# Revit family: RN 57035 Optifitt-Press-Übergang
name_source: partatom
category: Rohrformteile
units: mm (PartAtom-declared; Revit-internal decimal feet)

## family parameters
Arbeitsebenenbasiert = Nein
Beim Laden mit Abzugskörper schneiden = Nein
Bemaßung runder Anschluss = Durchmesser verwenden
Gemeinsam genutzt = Nein
Immer vertikal = Ja
Teiletyp = Verbindung

## types (8) — shared parameters
1.010.00.2 Blattnummer der Richtlinie = 29
1.010.00.3 Ausgabedatum (Monat) der Richtlinie = 201308
1.010.00.4 Herstellername = R. Nussbaum AG
1.010.00.5 Revisionsdatum der Datei = 20190521
1.010.00.6 Webadresse des Herstellers = http://www.nussbaum.ch
1.100.00.4 Produktbezeichnung = Versorgung
1.110.00.2 Index = 2
1.110.00.4 Produktbezeichnung = Optifitt-Press
1.960/3L.00.8 Link (URL) = https://www.nussbaum.ch
29.700.00.4 Produktname = Optifitt-Press-Übergang, mit Aussengewinde
29.700.00.5 Produktkennung = 2
29.700.00.6 Querschnittsform = 1
29.700.00.7 Nennweitensystem = DN
29.700.00.8 Nenndrucksystem = PN
29.710.02.4 Nenndruck = 16
29.710.02.5 max. zul. Überdruck [hPa] = 1600
29.710.02.7 max. zul. Dauer-Betriebsdruck [hPa] = 1600
29.710.02.9 max. zul. Dauer-Betriebstemperatur [°C] = 95
Beschreibung = Optifitt-Press-Übergang
Connector Visibility = Nein
EnclosingSpace Visibility = Nein
Hersteller = R. Nussbaum AG
URL = https://www.nussbaum.ch

## per-type parameters (varying)
- DN=50: 1.800.00.3 TGA-Nummer=01900200000000000000000000000000000000000000000014000000000000000008; 1.800.00.4 Kommentarfeld=57035.28, Optifitt-Press-Übergang, mit Aussengewinde, DN=50, L=104, R=2; 1.810.00.3 Hersteller-Bestellnummer=57035.28; 1.810.00.4 DATANORM-Nummer=57035.28; 1.810.00.5 StLB-Nummer=255.517; 1.810.00.6 GTIN-Nummer=7612945716620; 29.710.02.10 Formstück-Gewicht [kg]=0.681; 29.710.02.3 Benennung=Optifitt-Press-Übergang, mit Aussengewinde, DN=50, L=104, R=2; CONNECTOR0_DIAMETER_dX_0r=50 mm; CONNECTOR0_dX_01=50 mm; CONNECTOR0_ref_dX=50 mm; CONNECTOR1_DIAMETER_dX_0r=50 mm; CONNECTOR1_dX_00=80 mm; CONNECTOR1_dX_01=104 mm; CONNECTOR1_ref_dX=104 mm; Modell=57035.28; R. Nussbaum AG 57035.21 de Visibility=Nein; R. Nussbaum AG 57035.22 de Visibility=Nein; R. Nussbaum AG 57035.23 de Visibility=Nein; R. Nussbaum AG 57035.24 de Visibility=Nein; R. Nussbaum AG 57035.25 de Visibility=Nein; R. Nussbaum AG 57035.26 de Visibility=Nein; R. Nussbaum AG 57035.27 de Visibility=Nein; R. Nussbaum AG 57035.28 de Visibility=Ja; Typenkommentare=Optifitt-Press-Übergang  DN=50
- DN=40: 1.800.00.3 TGA-Nummer=01900200000000000000000000000000000000000000000014000000000000000007; 1.800.00.4 Kommentarfeld=57035.27, Optifitt-Press-Übergang, mit Aussengewinde, DN=40, L=95, R=1½; 1.810.00.3 Hersteller-Bestellnummer=57035.27; 1.810.00.4 DATANORM-Nummer=57035.27; 1.810.00.5 StLB-Nummer=255.516; 1.810.00.6 GTIN-Nummer=7612945716613; 29.710.02.10 Formstück-Gewicht [kg]=0.471; 29.710.02.3 Benennung=Optifitt-Press-Übergang, mit Aussengewinde, DN=40, L=95, R=1½; CONNECTOR0_DIAMETER_dX_0r=40 mm; CONNECTOR0_dX_01=48 mm; CONNECTOR0_ref_dX=48 mm; CONNECTOR1_DIAMETER_dX_0r=40 mm; CONNECTOR1_dX_00=78 mm; CONNECTOR1_dX_01=97 mm; CONNECTOR1_ref_dX=97 mm; Modell=57035.27; R. Nussbaum AG 57035.21 de Visibility=Nein; R. Nussbaum AG 57035.22 de Visibility=Nein; R. Nussbaum AG 57035.23 de Visibility=Nein; R. Nussbaum AG 57035.24 de Visibility=Nein; R. Nussbaum AG 57035.25 de Visibility=Nein; R. Nussbaum AG 57035.26 de Visibility=Nein; R. Nussbaum AG 57035.27 de Visibility=Ja; R. Nussbaum AG 57035.28 de Visibility=Nein; Typenkommentare=Optifitt-Press-Übergang  DN=40
- DN=32: 1.800.00.3 TGA-Nummer=01900200000000000000000000000000000000000000000014000000000000000006; 1.800.00.4 Kommentarfeld=57035.26, Optifitt-Press-Übergang, mit Aussengewinde, DN=32, L=92, R=1¼; 1.810.00.3 Hersteller-Bestellnummer=57035.26; 1.810.00.4 DATANORM-Nummer=57035.26; 1.810.00.5 StLB-Nummer=255.515; 1.810.00.6 GTIN-Nummer=7612945716606; 29.710.02.10 Formstück-Gewicht [kg]=0.369; 29.710.02.3 Benennung=Optifitt-Press-Übergang, mit Aussengewinde, DN=32, L=92, R=1¼; CONNECTOR0_DIAMETER_dX_0r=32 mm; CONNECTOR0_dX_01=46 mm; CONNECTOR0_ref_dX=46 mm; CONNECTOR1_DIAMETER_dX_0r=32 mm; CONNECTOR1_dX_00=75 mm; CONNECTOR1_dX_01=94 mm; CONNECTOR1_ref_dX=94 mm; Modell=57035.26; R. Nussbaum AG 57035.21 de Visibility=Nein; R. Nussbaum AG 57035.22 de Visibility=Nein; R. Nussbaum AG 57035.23 de Visibility=Nein; R. Nussbaum AG 57035.24 de Visibility=Nein; R. Nussbaum AG 57035.25 de Visibility=Nein; R. Nussbaum AG 57035.26 de Visibility=Ja; R. Nussbaum AG 57035.27 de Visibility=Nein; R. Nussbaum AG 57035.28 de Visibility=Nein; Typenkommentare=Optifitt-Press-Übergang  DN=32
- DN=25: 1.800.00.3 TGA-Nummer=01900200000000000000000000000000000000000000000014000000000000000005; 1.800.00.4 Kommentarfeld=57035.25, Optifitt-Press-Übergang, mit Aussengewinde, DN=25, L=78, R=1; 1.810.00.3 Hersteller-Bestellnummer=57035.25; 1.810.00.4 DATANORM-Nummer=57035.25; 1.810.00.5 StLB-Nummer=255.514; 1.810.00.6 GTIN-Nummer=7612945716491; 29.710.02.10 Formstück-Gewicht [kg]=0.239; 29.710.02.3 Benennung=Optifitt-Press-Übergang, mit Aussengewinde, DN=25, L=78, R=1; CONNECTOR0_DIAMETER_dX_0r=25 mm  [stored 0.082021 ft]; CONNECTOR0_dX_01=34 mm; CONNECTOR0_ref_dX=34 mm; CONNECTOR1_DIAMETER_dX_0r=25 mm  [stored 0.082021 ft]; CONNECTOR1_dX_00=61 mm; CONNECTOR1_dX_01=78 mm; CONNECTOR1_ref_dX=78 mm; Modell=57035.25; R. Nussbaum AG 57035.21 de Visibility=Nein; R. Nussbaum AG 57035.22 de Visibility=Nein; R. Nussbaum AG 57035.23 de Visibility=Nein; R. Nussbaum AG 57035.24 de Visibility=Nein; R. Nussbaum AG 57035.25 de Visibility=Ja; R. Nussbaum AG 57035.26 de Visibility=Nein; R. Nussbaum AG 57035.27 de Visibility=Nein; R. Nussbaum AG 57035.28 de Visibility=Nein; Typenkommentare=Optifitt-Press-Übergang  DN=25
- DN=20: 1.800.00.3 TGA-Nummer=01900200000000000000000000000000000000000000000014000000000000000004; 1.800.00.4 Kommentarfeld=57035.24, Optifitt-Press-Übergang, mit Aussengewinde, DN=20, L=70, R=¾; 1.810.00.3 Hersteller-Bestellnummer=57035.24; 1.810.00.4 DATANORM-Nummer=57035.24; 1.810.00.5 StLB-Nummer=255.513; 1.810.00.6 GTIN-Nummer=7612945716484; 29.710.02.10 Formstück-Gewicht [kg]=0.147; 29.710.02.3 Benennung=Optifitt-Press-Übergang, mit Aussengewinde, DN=20, L=70, R=¾; CONNECTOR0_DIAMETER_dX_0r=20 mm; CONNECTOR0_dX_01=29 mm; CONNECTOR0_ref_dX=29 mm; CONNECTOR1_DIAMETER_dX_0r=20 mm; CONNECTOR1_dX_00=55 mm; CONNECTOR1_dX_01=70 mm; CONNECTOR1_ref_dX=70 mm; Modell=57035.24; R. Nussbaum AG 57035.21 de Visibility=Nein; R. Nussbaum AG 57035.22 de Visibility=Nein; R. Nussbaum AG 57035.23 de Visibility=Nein; R. Nussbaum AG 57035.24 de Visibility=Ja; R. Nussbaum AG 57035.25 de Visibility=Nein; R. Nussbaum AG 57035.26 de Visibility=Nein; R. Nussbaum AG 57035.27 de Visibility=Nein; R. Nussbaum AG 57035.28 de Visibility=Nein; Typenkommentare=Optifitt-Press-Übergang  DN=20
- DN=15: 1.800.00.3 TGA-Nummer=01900200000000000000000000000000000000000000000014000000000000000003; 1.800.00.4 Kommentarfeld=57035.23, Optifitt-Press-Übergang, mit Aussengewinde, DN=15, L=64, R=½; 1.810.00.3 Hersteller-Bestellnummer=57035.23; 1.810.00.4 DATANORM-Nummer=57035.23; 1.810.00.5 StLB-Nummer=255.512; 1.810.00.6 GTIN-Nummer=7612945716477; 29.710.02.10 Formstück-Gewicht [kg]=0.106; 29.710.02.3 Benennung=Optifitt-Press-Übergang, mit Aussengewinde, DN=15, L=64, R=½; CONNECTOR0_DIAMETER_dX_0r=15 mm; CONNECTOR0_dX_01=27 mm; CONNECTOR0_ref_dX=27 mm; CONNECTOR1_DIAMETER_dX_0r=15 mm; CONNECTOR1_dX_00=51 mm; CONNECTOR1_dX_01=64 mm; CONNECTOR1_ref_dX=64 mm; Modell=57035.23; R. Nussbaum AG 57035.21 de Visibility=Nein; R. Nussbaum AG 57035.22 de Visibility=Nein; R. Nussbaum AG 57035.23 de Visibility=Ja; R. Nussbaum AG 57035.24 de Visibility=Nein; R. Nussbaum AG 57035.25 de Visibility=Nein; R. Nussbaum AG 57035.26 de Visibility=Nein; R. Nussbaum AG 57035.27 de Visibility=Nein; R. Nussbaum AG 57035.28 de Visibility=Nein; Typenkommentare=Optifitt-Press-Übergang  DN=15
- DN=1: 1.800.00.3 TGA-Nummer=01900200000000000000000000000000000000000000000014000000000000000002; 1.800.00.4 Kommentarfeld=57035.22, Optifitt-Press-Übergang, mit Aussengewinde, DN=10, L=61, R=½; 1.810.00.3 Hersteller-Bestellnummer=57035.22; 1.810.00.4 DATANORM-Nummer=57035.22; 1.810.00.6 GTIN-Nummer=7612945741332; 29.710.02.10 Formstück-Gewicht [kg]=0.082; 29.710.02.3 Benennung=Optifitt-Press-Übergang, mit Aussengewinde, DN=10, L=61, R=½; CONNECTOR0_DIAMETER_dX_0r=10 mm  [stored 0.0328084 ft]; CONNECTOR0_dX_01=24 mm; CONNECTOR0_ref_dX=24 mm; CONNECTOR1_DIAMETER_dX_0r=15 mm; CONNECTOR1_dX_00=48 mm; CONNECTOR1_dX_01=61 mm; CONNECTOR1_ref_dX=61 mm; Modell=57035.22; R. Nussbaum AG 57035.21 de Visibility=Nein; R. Nussbaum AG 57035.22 de Visibility=Ja; R. Nussbaum AG 57035.23 de Visibility=Nein; R. Nussbaum AG 57035.24 de Visibility=Nein; R. Nussbaum AG 57035.25 de Visibility=Nein; R. Nussbaum AG 57035.26 de Visibility=Nein; R. Nussbaum AG 57035.27 de Visibility=Nein; R. Nussbaum AG 57035.28 de Visibility=Nein; Typenkommentare=Optifitt-Press-Übergang  DN=10
- DN=10: 1.800.00.3 TGA-Nummer=01900200000000000000000000000000000000000000000014000000000000000001; 1.800.00.4 Kommentarfeld=57035.21, Optifitt-Press-Übergang, mit Aussengewinde, DN=10, L=57, R=3/8; 1.810.00.3 Hersteller-Bestellnummer=57035.21; 1.810.00.4 DATANORM-Nummer=57035.21; 1.810.00.6 GTIN-Nummer=7612945741325; 29.710.02.10 Formstück-Gewicht [kg]=0.073; 29.710.02.3 Benennung=Optifitt-Press-Übergang, mit Aussengewinde, DN=10, L=57, R=3/8; CONNECTOR0_DIAMETER_dX_0r=10 mm  [stored 0.0328084 ft]; CONNECTOR0_dX_01=24 mm; CONNECTOR0_ref_dX=24 mm; CONNECTOR1_DIAMETER_dX_0r=10 mm  [stored 0.0328084 ft]; CONNECTOR1_dX_00=47 mm; CONNECTOR1_dX_01=57 mm; CONNECTOR1_ref_dX=57 mm; Modell=57035.21; R. Nussbaum AG 57035.21 de Visibility=Ja; R. Nussbaum AG 57035.22 de Visibility=Nein; R. Nussbaum AG 57035.23 de Visibility=Nein; R. Nussbaum AG 57035.24 de Visibility=Nein; R. Nussbaum AG 57035.25 de Visibility=Nein; R. Nussbaum AG 57035.26 de Visibility=Nein; R. Nussbaum AG 57035.27 de Visibility=Nein; R. Nussbaum AG 57035.28 de Visibility=Nein; Typenkommentare=Optifitt-Press-Übergang  DN=10

note: [stored X ft] marks values corroborated as IEEE doubles in the binary element streams (Revit-internal decimal feet)

## geometry (parser evidence)
native form markers: Sweep x2
no freeform markers — native parametric forms only
